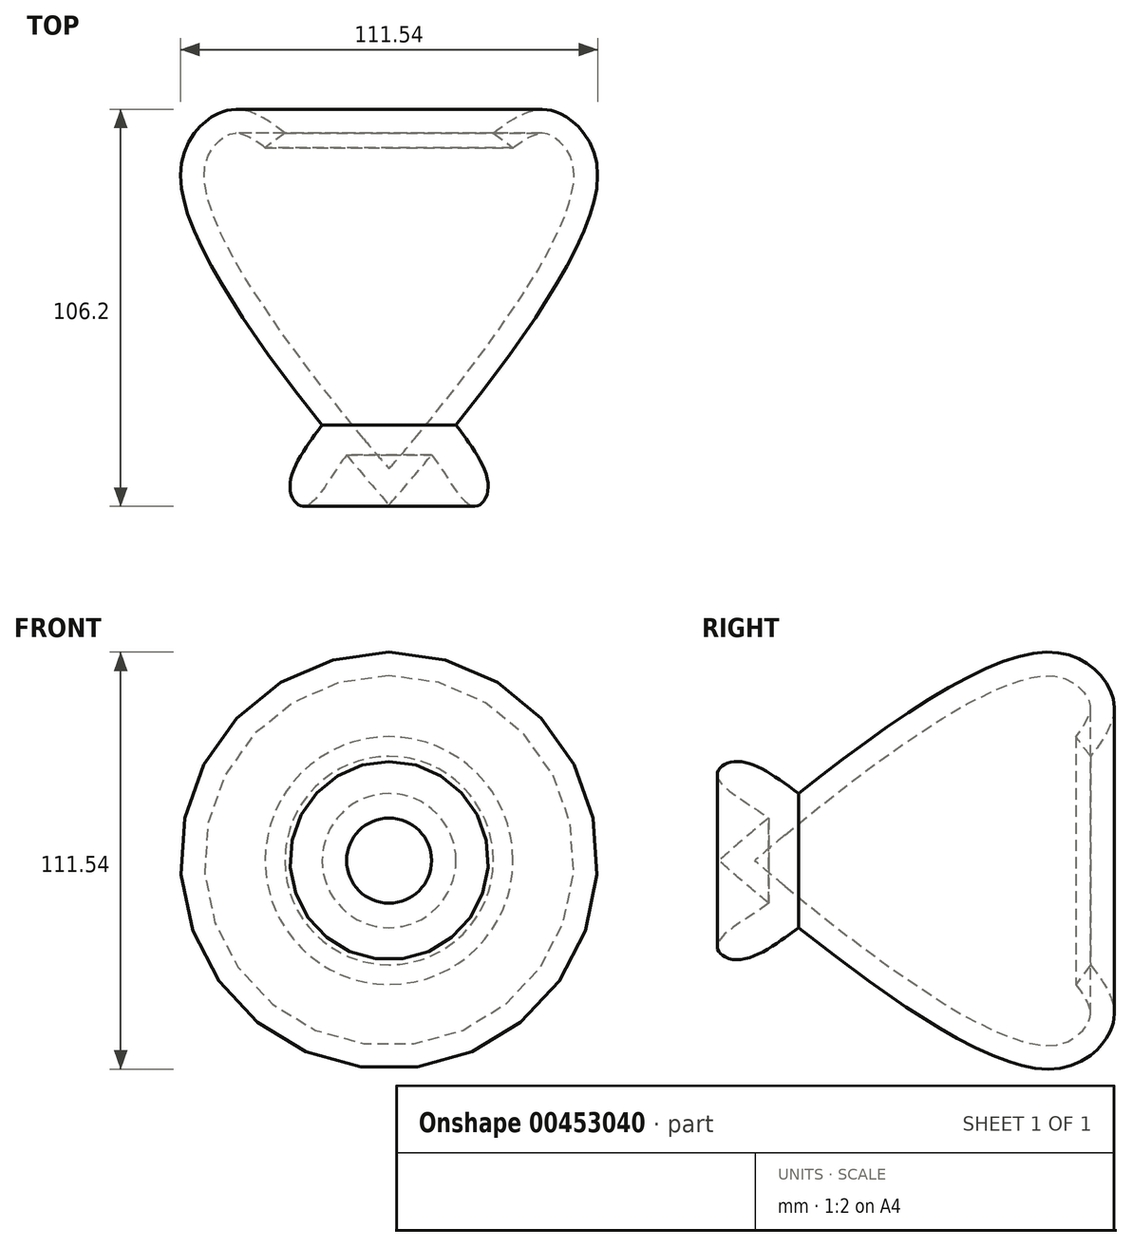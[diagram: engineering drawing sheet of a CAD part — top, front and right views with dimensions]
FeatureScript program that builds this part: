
annotation { "Feature Type Name" : "Feature", "Feature Type Description" : "" }
export const myFeature = defineFeature(function(context is Context, id is Id, definition is map)
    precondition{}
    {
        {
            var Q0;
            Q0=qCreatedBy(makeId("Top.planeOp"),FACE);
            var sketch = newSketch(context, id + "F0", { "sketchPlane" : qUnion([Q0])});
            skLineSegment(sketch, "E0", {"start": v(0, 54.71) * mm, "end": v(0, -55.9) * mm});
            skFitSpline(sketch, "E1", {"points": [v(0, -55.9) * mm, v(55.17, 26.7) * mm, v(50.9, 45) * mm, v(39.93, 49.87) * mm, v(25, 41.34) * mm], "startDerivative": vector(170.42, 195.39) * mm, "endDerivative": vector(-79.07, -62.94) * mm});
            skFitSpline(sketch, "E2.0", {"points": [v(-4.79, -51.72) * mm, v(-1.26, -47.68) * mm, v(5.76, -39.46) * mm, v(15.89, -27) * mm, v(25.3, -14.7) * mm, v(33.63, -2.84) * mm, v(40.57, 8.23) * mm, v(44.9, 16.5) * mm, v(47.02, 21.6) * mm, v(47.96, 24.26) * mm, v(48.52, 26.13) * mm, v(48.87, 27.56) * mm, v(49.08, 28.62) * mm, v(49.33, 30.16) * mm, v(49.48, 32.22) * mm, v(49.3, 34.5) * mm, v(48.85, 36.4) * mm, v(48.28, 37.77) * mm, v(47.71, 38.78) * mm, v(47.24, 39.5) * mm, v(46.8, 40.06) * mm, v(46.4, 40.5) * mm, v(46, 40.94) * mm, v(45.5, 41.44) * mm, v(44.66, 42.15) * mm, v(43.82, 42.7) * mm, v(43.03, 43.1) * mm, v(42.46, 43.32) * mm, v(41.93, 43.47) * mm, v(41.44, 43.56) * mm, v(41.05, 43.58) * mm, v(40.75, 43.57) * mm, v(40.53, 43.55) * mm, v(40.28, 43.52) * mm, v(39.91, 43.44) * mm, v(39.38, 43.3) * mm, v(38.62, 43.01) * mm, v(37.49, 42.49) * mm, v(35.87, 41.56) * mm, v(33.7, 40.08) * mm, v(31.4, 38.32) * mm, v(29.77, 37.03) * mm, v(28.95, 36.37) * mm]});
            skFitSpline(sketch, "E3", {"points": [v(14.02, -29.41) * mm, v(26.52, -51.05) * mm, v(22.56, -56.24) * mm, v(11.37, -42.54) * mm, v(6.1, -37.64) * mm], "startDerivative": vector(52, -68.95) * mm, "endDerivative": vector(-11.76, 10.98) * mm});
            skLineSegment(sketch, "E4", {"start": v(27.88, 43.61) * mm, "end": v(33.17, 39.66) * mm});
            skPoint(sketch, "E5.orphan", {"position": v(25.6, 45.31) * mm});
            skSolve(sketch);
        }
        {
            var Q0;
            {var subQ0=sQuery(id+"F0.wireOp",EDGE,"E1");var subQ1=sQuery(id+"F0.wireOp",EDGE,"E0");var subQ2=makeQuery(id+"F0.imprint","INTERSECT",VERTEX,{"derivedFrom":[subQ1,subQ0]});Q0=makeQuery(id+"F0.imprint","IMPRINT",FACE,{"disambiguationData":[TD([[makeQuery(id+"F0.imprint","IMPRINT",EDGE,{"disambiguationData":[TD([[subQ2,1.0]])],"derivedFrom":subQ1}),1.0]])]});}
            var Q1;
            Q1=sQuery(id+"F0.wireOp",EDGE,"E0");
            revolve(context, id + "F1", {"entities" : qUnion([Q0]), "axis" : qUnion([Q1]), "revolveType" : RevolveType.FULL});
        }
        {
            var Q0;
            Q0 = qSketchRegion(id + "F0", true);
            var Q1;
            Q1=makeQuery(id+"F1.opRevolve","SWEPT_FACE",FACE,{"disambiguationData":[OSD([sQuery(id+"F0.wireOp",EDGE,"E1")])]});
            revolve(context, id + "F2", {"operationType" : NewBodyOperationType.ADD, "entities" : qUnion([Q0]), "axis" : qUnion([Q1]), "revolveType" : RevolveType.FULL});
        }
    });
